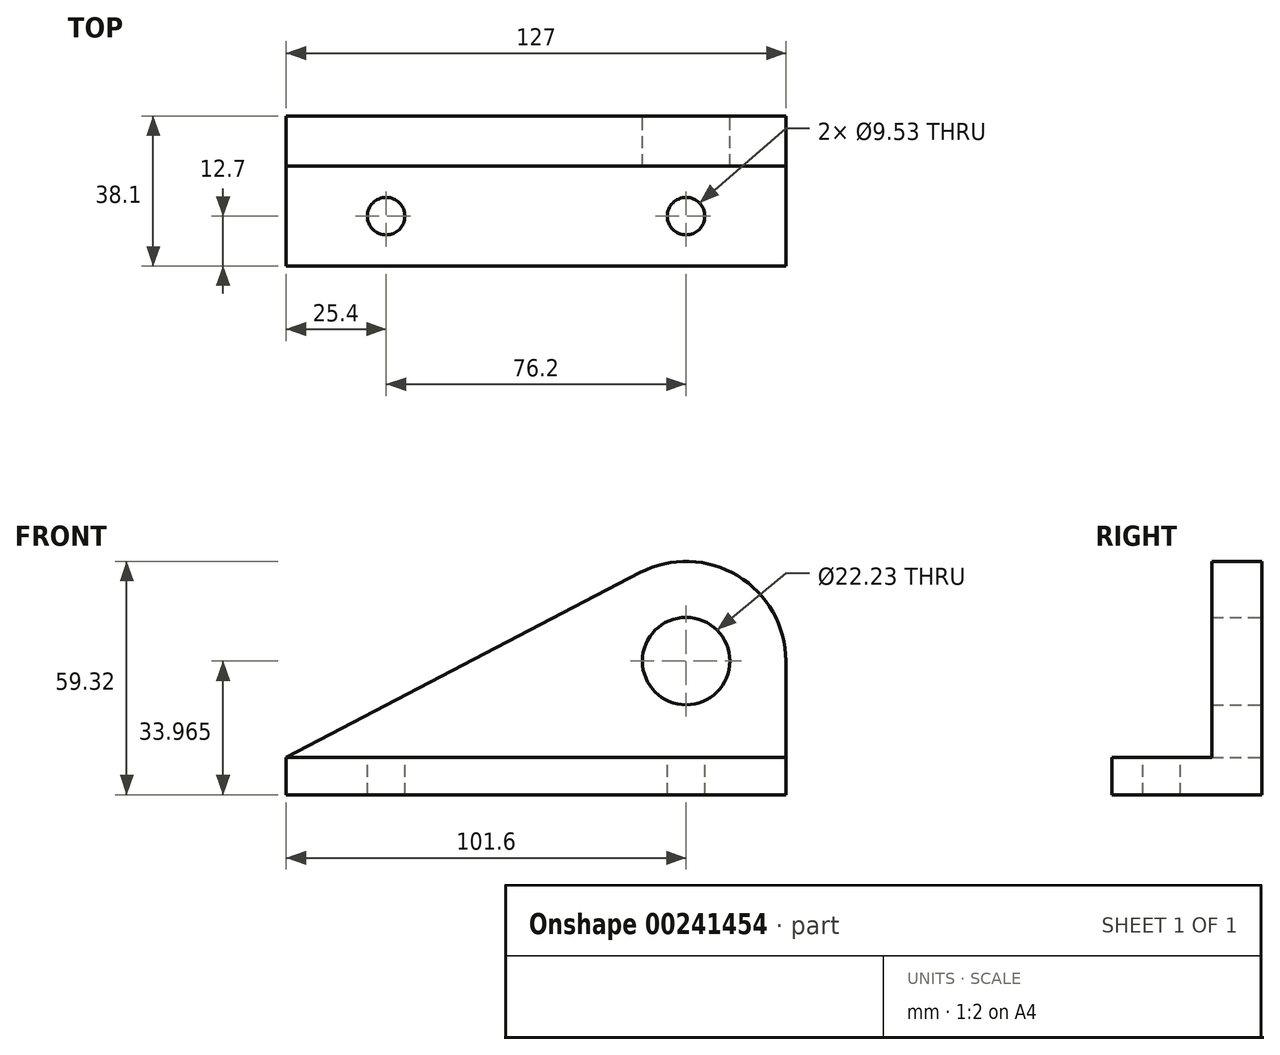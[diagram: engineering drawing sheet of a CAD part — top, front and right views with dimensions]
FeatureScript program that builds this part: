
annotation { "Feature Type Name" : "Feature", "Feature Type Description" : "" }
export const myFeature = defineFeature(function(context is Context, id is Id, definition is map)
    precondition{}
    {
        {
            var Q0;
            Q0=qCreatedBy(makeId("Front.planeOp"),FACE);
            var sketch = newSketch(context, id + "F0", { "sketchPlane" : qUnion([Q0])});
            skLineSegment(sketch, "E0", {"start": v(0, 0) * mm, "end": v(127, 0) * mm});
            skLineSegment(sketch, "E1", {"start": v(127, 0) * mm, "end": v(127, 9.52) * mm});
            skLineSegment(sketch, "E2", {"start": v(0, 0) * mm, "end": v(0, 9.52) * mm});
            skLineSegment(sketch, "E3", {"start": v(0, 9.52) * mm, "end": v(127, 9.52) * mm});
            skLineSegment(sketch, "E4", {"start": v(127, 9.52) * mm, "end": v(126.95, 34.01) * mm});
            skLineSegment(sketch, "E5", {"start": v(0, 9.52) * mm, "end": v(89.87, 56.44) * mm});
            skArc(sketch, "E6.trimOffspring", {"start": v(126.95, 34.01) * mm, "mid": v(114.72, 55.66) * mm, "end": v(89.87, 56.44) * mm});
            skPoint(sketch, "E7.start.orphan", {"position": v(101.6, 9.52) * mm});
            skSolve(sketch);
        }
        {
            var Q0;
            Q0=makeQuery(id+"F0.imprint","IMPRINT",FACE,{"disambiguationData":[TD([[makeQuery(id+"F0.imprint","IMPRINT",EDGE,{"derivedFrom":sQuery(id+"F0.wireOp",EDGE,"E0")}),1.0]])]});
            extrude(context, id + "F1", {"entities" : qUnion([Q0]), "depth" : 38.1 * mm});
        }
        {
            var Q0;
            Q0=makeQuery(id+"F0.imprint","IMPRINT",FACE,{"disambiguationData":[TD([[makeQuery(id+"F0.imprint","IMPRINT",EDGE,{"derivedFrom":sQuery(id+"F0.wireOp",EDGE,"E3")}),1.0]])]});
            extrude(context, id + "F2", {"entities" : qUnion([Q0]), "operationType" : NewBodyOperationType.ADD, "depth" : 12.7 * mm});
        }
        {
            var Q0;
            Q0=sQuery(id+"F0.wireOp",VERTEX,"E6.trimOffspring.center");
            var Q1;
            Q1=makeQuery(id+"F1.opExtrude","SWEPT_BODY",BODY,{"disambiguationData":[OSD([sQuery(id+"F0.wireOp",EDGE,"E0"),sQuery(id+"F0.wireOp",EDGE,"E1"),sQuery(id+"F0.wireOp",EDGE,"E2"),sQuery(id+"F0.wireOp",EDGE,"E3")])]});
            hole(context, id + "F3", {"style" : HoleStyle.SIMPLE, "endStyle" : HoleEndStyle.THROUGH, "oppositeDirection" : true, "holeDiameter" : 22.22 * mm, "locations" : qUnion([Q0]), "scope" : qUnion([Q1]), "isTappedThrough" : true});
        }
        {
            var Q0;
            Q0=makeQuery(id+"F1.opExtrude","SWEPT_FACE",FACE,{"disambiguationData":[OSD([sQuery(id+"F0.wireOp",EDGE,"E3")])]});
            var sketch = newSketch(context, id + "F4", { "sketchPlane" : qUnion([Q0])});
            skLineSegment(sketch, "E8", {"start": v(0, -12.7) * mm, "end": v(0, -38.1) * mm});
            skLineSegment(sketch, "E9", {"start": v(0, -12.7) * mm, "end": v(0, -25.4) * mm});
            skLineSegment(sketch, "E10", {"start": v(0, -25.4) * mm, "end": v(25.4, -25.4) * mm});
            skLineSegment(sketch, "E11", {"start": v(25.4, -25.4) * mm, "end": v(101.6, -25.4) * mm});
            skSolve(sketch);
        }
        {
            var Q0;
            Q0=sQuery(id+"F4.wireOp",VERTEX,"E11.start");
            var Q1;
            Q1=sQuery(id+"F4.wireOp",VERTEX,"E11.end");
            var Q2;
            Q2=makeQuery(id+"F1.opExtrude","SWEPT_BODY",BODY,{"disambiguationData":[OSD([sQuery(id+"F0.wireOp",EDGE,"E0"),sQuery(id+"F0.wireOp",EDGE,"E1"),sQuery(id+"F0.wireOp",EDGE,"E2"),sQuery(id+"F0.wireOp",EDGE,"E3")])]});
            hole(context, id + "F5", {"style" : HoleStyle.SIMPLE, "endStyle" : HoleEndStyle.THROUGH, "holeDiameter" : 9.52 * mm, "locations" : qUnion([Q0, Q1]), "scope" : qUnion([Q2]), "isTappedThrough" : true});
        }
    });
